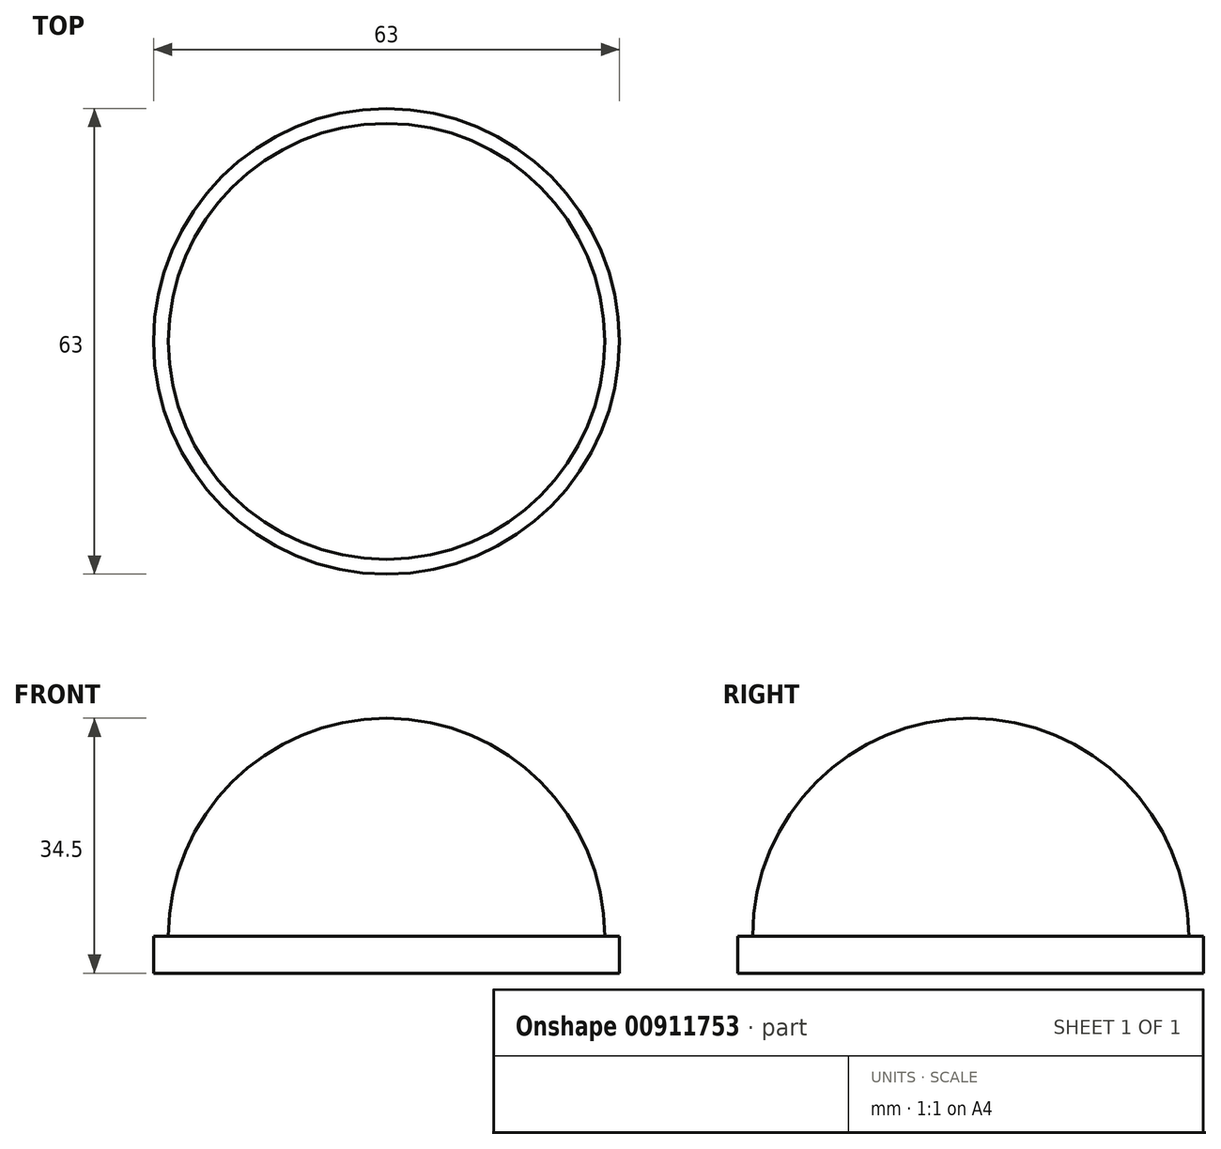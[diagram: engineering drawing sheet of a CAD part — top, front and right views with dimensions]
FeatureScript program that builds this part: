
annotation { "Feature Type Name" : "Feature", "Feature Type Description" : "" }
export const myFeature = defineFeature(function(context is Context, id is Id, definition is map)
    precondition{}
    {
        {
            var Q0;
            Q0=qCreatedBy(makeId("Top.planeOp"),FACE);
            var sketch = newSketch(context, id + "F0", { "sketchPlane" : qUnion([Q0])});
            skCircle(sketch, "E0", {"center": v(0, 0) * mm, "radius": 29.5 * mm});
            skLineSegment(sketch, "E1", {"start": v(0, 29.5) * mm, "end": v(0, -29.5) * mm});
            skSolve(sketch);
        }
        {
            var Q0;
            {var subQ0=sQuery(id+"F0.wireOp",EDGE,"E1");Q0=makeQuery(id+"F0.imprint","IMPRINT",FACE,{"disambiguationData":[TD([[makeQuery(id+"F0.imprint","IMPRINT",EDGE,{"derivedFrom":subQ0}),1.0]])]});}
            var Q1;
            Q1=sQuery(id+"F0.wireOp",EDGE,"E1");
            revolve(context, id + "F1", {"surfaceOperationType" : NewSurfaceOperationType.NEW, "entities" : qUnion([Q0]), "axis" : qUnion([Q1]), "revolveType" : RevolveType.ONE_DIRECTION, "angle" : 180 * degree});
        }
        {
            var Q0;
            Q0=makeQuery(id+"F1.opRevolve","CAP_FACE",FACE,{"disambiguationData":[OSD([sQuery(id+"F0.wireOp",EDGE,"E0"),sQuery(id+"F0.wireOp",EDGE,"E1")])],"isStart":true});
            var sketch = newSketch(context, id + "F2", { "sketchPlane" : qUnion([Q0])});
            skCircle(sketch, "E2", {"center": v(0, 0) * mm, "radius": 31.5 * mm});
            skSolve(sketch);
        }
        {
            var Q0;
            Q0=qSketchRegion(id+"F2",true);
            extrude(context, id + "F3", {"entities" : qUnion([Q0]), "operationType" : NewBodyOperationType.ADD, "depth" : 5 * mm, "offsetDistance" : 25 * mm});
        }
    });
